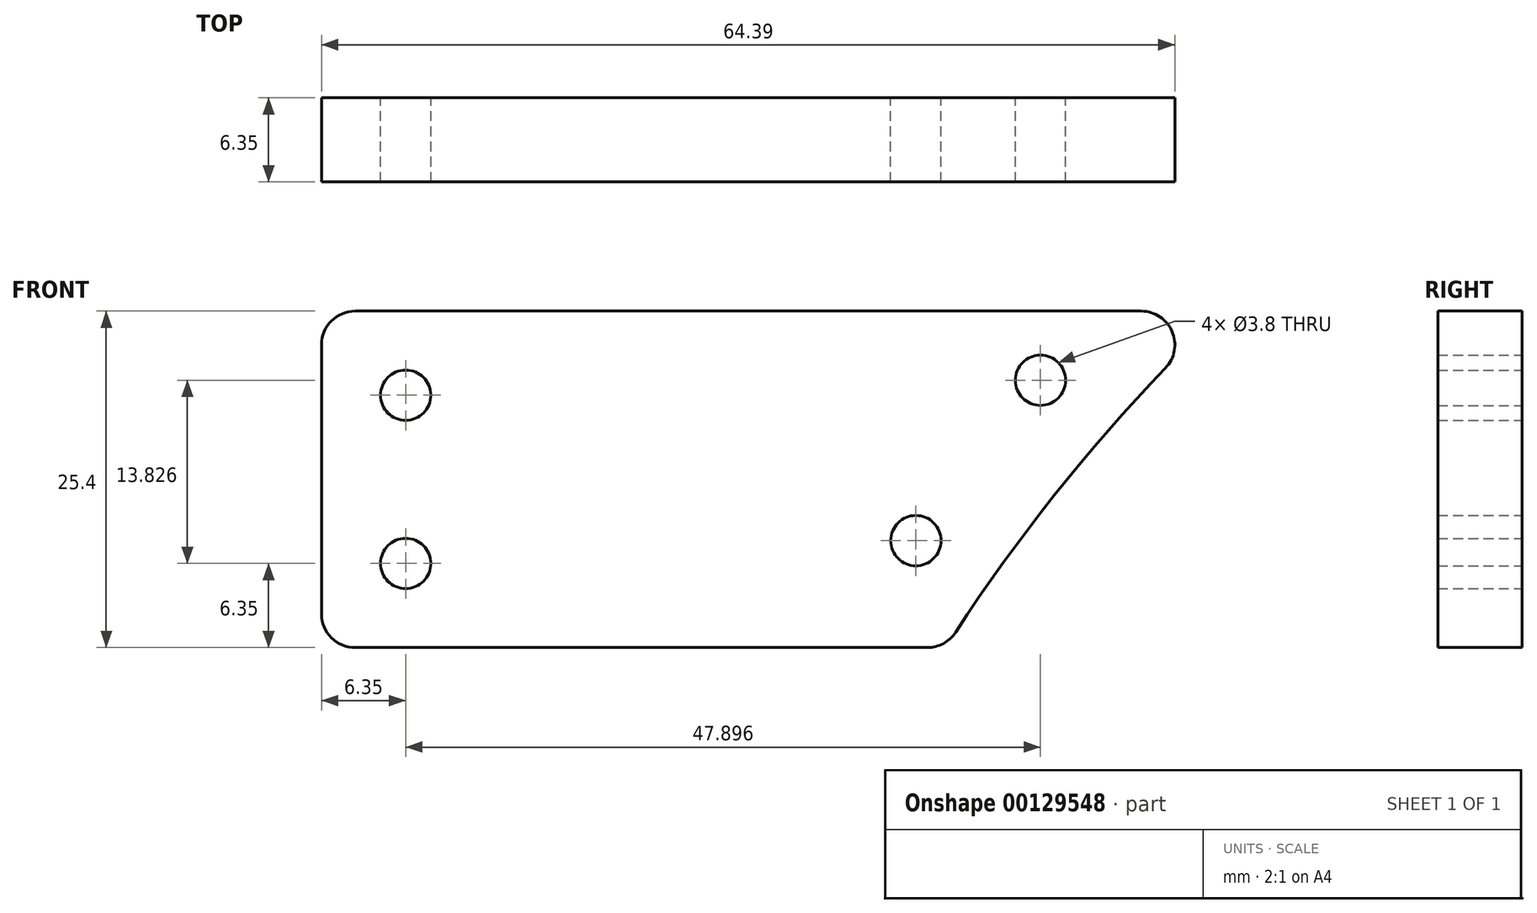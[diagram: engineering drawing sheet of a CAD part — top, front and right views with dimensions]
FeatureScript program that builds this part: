
annotation { "Feature Type Name" : "Feature", "Feature Type Description" : "" }
export const myFeature = defineFeature(function(context is Context, id is Id, definition is map)
    precondition{}
    {
        {
            var Q0;
            Q0=qCreatedBy(makeId("Front.planeOp"),FACE);
            var sketch = newSketch(context, id + "F0", { "sketchPlane" : qUnion([Q0])});
            skLineSegment(sketch, "E0.bottom", {"start": v(-25.4, 12.7) * mm, "end": v(25.4, 12.7) * mm});
            skLineSegment(sketch, "E0.top", {"start": v(-25.4, -12.7) * mm, "end": v(21.7, -12.7) * mm});
            skLineSegment(sketch, "E0.left", {"start": v(-25.4, 12.7) * mm, "end": v(-25.4, -12.7) * mm});
            skPoint(sketch, "E0.middle", {"position": v(0, 0) * mm});
            skArc(sketch, "E1", {"start": v(42.6, 12.7) * mm, "mid": v(31.38, 0.63) * mm, "end": v(21.7, -12.7) * mm});
            skPoint(sketch, "E2.orphan", {"position": v(25.4, -12.7) * mm});
            skLineSegment(sketch, "E3", {"start": v(25.4, 12.7) * mm, "end": v(42.6, 12.7) * mm});
            skCircle(sketch, "E4", {"center": v(-19.05, 6.35) * mm, "radius": 1.9 * mm});
            skLineSegment(sketch, "E5", {"start": v(-19.05, 12.7) * mm, "end": v(-19.05, -12.7) * mm, "construction": true});
            skCircle(sketch, "E6.MirrorC", {"center": v(-19.05, -6.35) * mm, "radius": 1.9 * mm});
            skCircle(sketch, "E7", {"center": v(28.85, 7.48) * mm, "radius": 1.9 * mm});
            skCircle(sketch, "E8", {"center": v(19.44, -4.63) * mm, "radius": 1.9 * mm});
            skSolve(sketch);
        }
        {
            var Q0;
            Q0 = qSketchRegion(id + "F0", true);
            extrude(context, id + "F1", {"entities" : qUnion([Q0]), "depth" : 6.35 * mm});
        }
        {
            var Q0;
            Q0=makeQuery(id+"F1.opExtrude","SWEPT_EDGE",EDGE,{"disambiguationData":[OSD([sQuery(id+"F0.wireOp",EDGE,"E0.bottom"),sQuery(id+"F0.wireOp",EDGE,"E0.left")])]});
            var Q1;
            Q1=makeQuery(id+"F1.opExtrude","SWEPT_EDGE",EDGE,{"disambiguationData":[OSD([sQuery(id+"F0.wireOp",EDGE,"E0.top"),sQuery(id+"F0.wireOp",EDGE,"E0.left")])]});
            var Q2;
            Q2=makeQuery(id+"F1.opExtrude","SWEPT_EDGE",EDGE,{"disambiguationData":[OSD([sQuery(id+"F0.wireOp",EDGE,"E3"),sQuery(id+"F0.wireOp",EDGE,"E1")])]});
            var Q3;
            Q3=makeQuery(id+"F1.opExtrude","SWEPT_EDGE",EDGE,{"disambiguationData":[OSD([sQuery(id+"F0.wireOp",EDGE,"E0.top"),sQuery(id+"F0.wireOp",EDGE,"E1")])]});
            fillet(context, id + "F2", {"entities" : qUnion([Q0, Q1, Q2, Q3]), "radius" : 2.54 * mm, "tangentPropagation" : true, "allowEdgeOverflow" : false});
        }
    });
